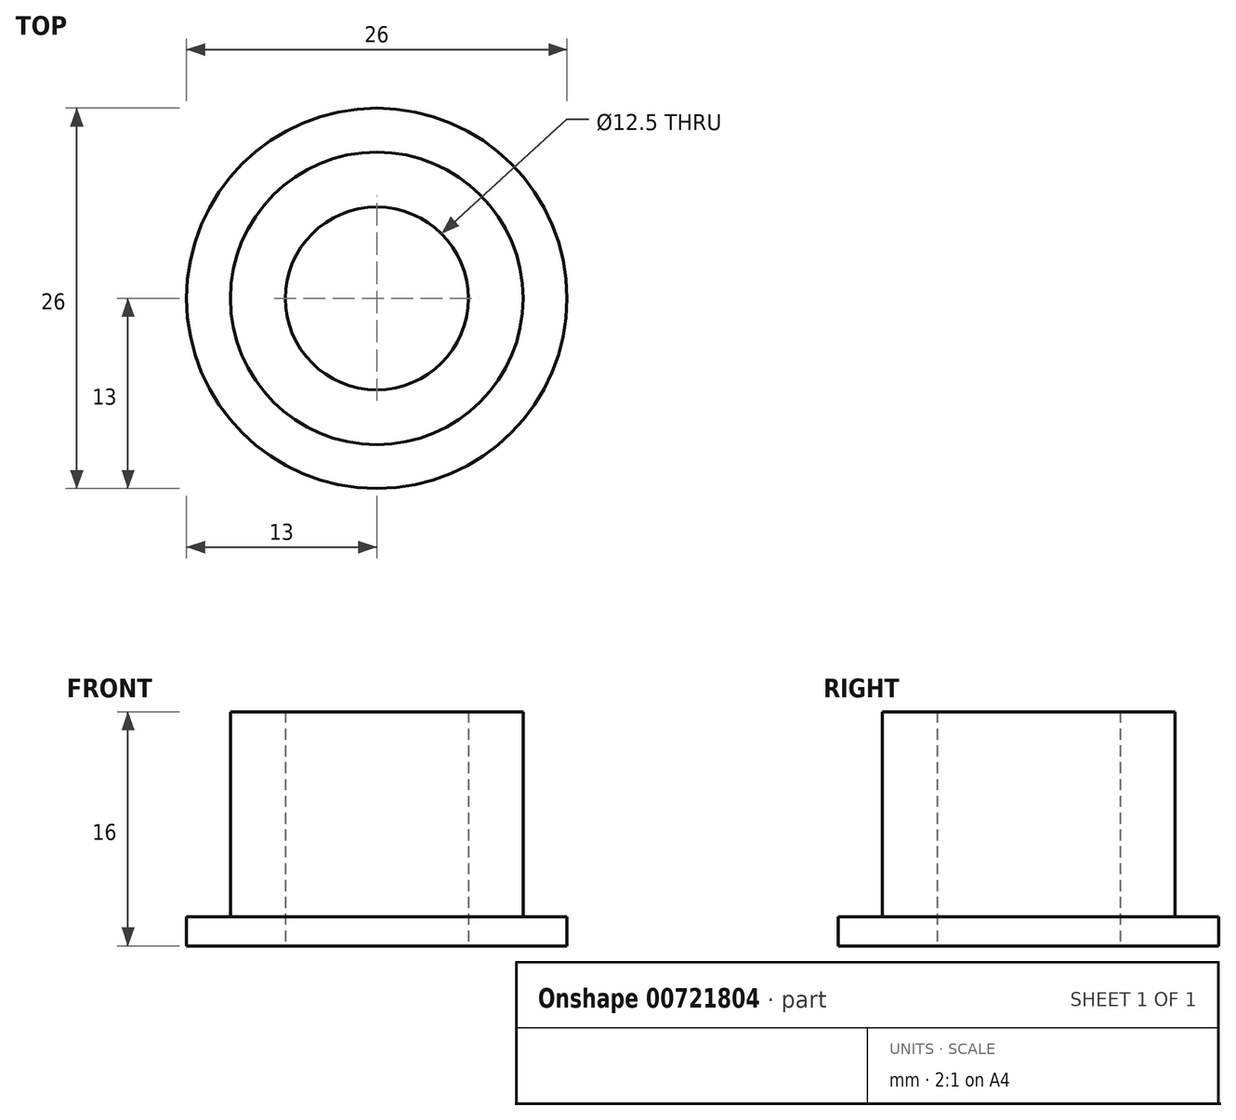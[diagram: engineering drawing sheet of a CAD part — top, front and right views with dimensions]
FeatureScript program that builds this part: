
annotation { "Feature Type Name" : "Feature", "Feature Type Description" : "" }
export const myFeature = defineFeature(function(context is Context, id is Id, definition is map)
    precondition{}
    {
        {
            var Q0;
            Q0=qCreatedBy(makeId("Top.planeOp"),FACE);
            var sketch = newSketch(context, id + "F0", { "sketchPlane" : qUnion([Q0])});
            skLineSegment(sketch, "E0", {"start": v(0, 0) * mm, "end": v(5.07, 3.66) * mm});
            skCircle(sketch, "E1", {"center": v(0, 0) * mm, "radius": 6.25 * mm});
            skLineSegment(sketch, "E2", {"start": v(0, 0) * mm, "end": v(-10.97, 6.97) * mm});
            skCircle(sketch, "E3", {"center": v(0, 0) * mm, "radius": 13 * mm});
            skLineSegment(sketch, "E4", {"start": v(0, 0) * mm, "end": v(-2.19, 9.76) * mm});
            skCircle(sketch, "E5", {"center": v(0, 0) * mm, "radius": 10 * mm});
            skSolve(sketch);
        }
        {
            var Q0;
            Q0=makeQuery(id+"F0.imprint","IMPRINT",FACE,{"disambiguationData":[TD([[makeQuery(id+"F0.imprint","IMPRINT",EDGE,{"derivedFrom":sQuery(id+"F0.wireOp",EDGE,"E3")}),1.0]])]});
            extrude(context, id + "F1", {"entities" : qUnion([Q0]), "depth" : 2 * mm, "offsetDistance" : 25.4 * mm});
        }
        {
            var Q0;
            {var subQ3=sQuery(id+"F0.wireOp",EDGE,"E1");var subQ8=makeQuery(id+"F0.imprint","INTERSECT",VERTEX,{"derivedFrom":[sQuery(id+"F0.wireOp",EDGE,"E0"),subQ3]});Q0=makeQuery(id+"F0.imprint","IMPRINT",FACE,{"disambiguationData":[TD([[makeQuery(id+"F0.imprint","IMPRINT",EDGE,{"disambiguationData":[TD([[subQ8,-1.0]])],"derivedFrom":subQ3}),-1.0]])]});}
            var Q1;
            {var subQ0=sQuery(id+"F0.wireOp",EDGE,"E4");var subQ1=sQuery(id+"F0.wireOp",EDGE,"E1");var subQ2=makeQuery(id+"F0.imprint","INTERSECT",VERTEX,{"derivedFrom":[subQ1,subQ0]});Q1=makeQuery(id+"F0.imprint","IMPRINT",FACE,{"disambiguationData":[TD([[makeQuery(id+"F0.imprint","IMPRINT",EDGE,{"disambiguationData":[TD([[subQ2,-1.0]])],"derivedFrom":subQ1}),-1.0]])]});}
            extrude(context, id + "F2", {"entities" : qUnion([Q0, Q1]), "operationType" : NewBodyOperationType.ADD, "depth" : 16 * mm, "offsetDistance" : 25.4 * mm});
        }
    });
